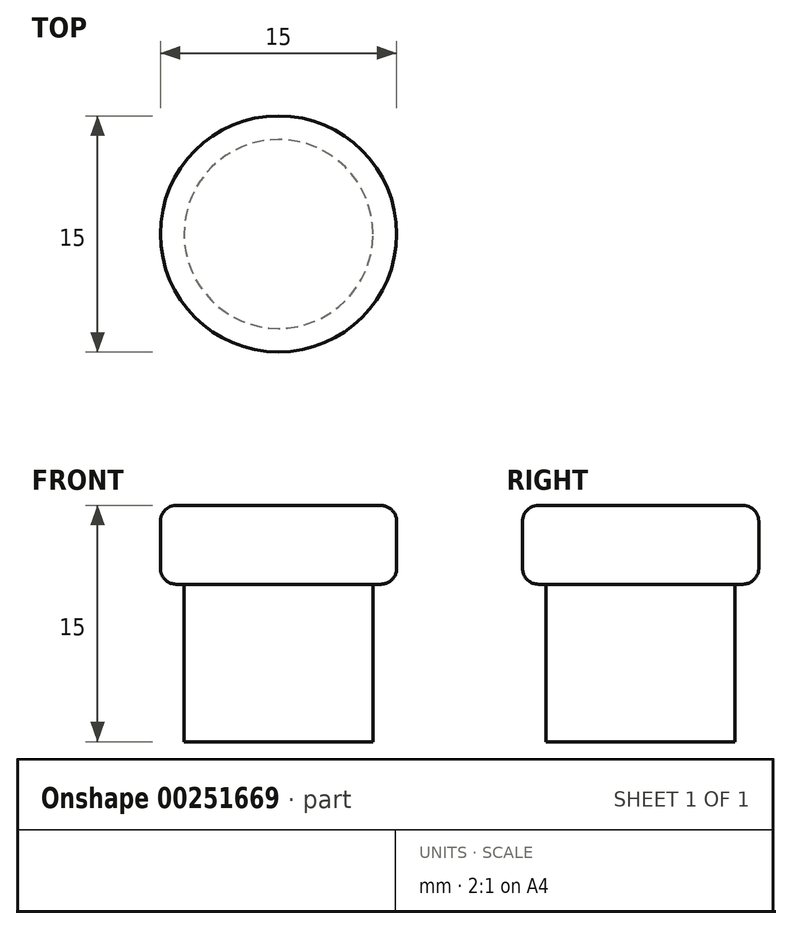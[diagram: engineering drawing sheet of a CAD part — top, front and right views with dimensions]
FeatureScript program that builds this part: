
annotation { "Feature Type Name" : "Feature", "Feature Type Description" : "" }
export const myFeature = defineFeature(function(context is Context, id is Id, definition is map)
    precondition{}
    {
        {
            var Q0;
            Q0=qCreatedBy(makeId("Top.planeOp"),FACE);
            var sketch = newSketch(context, id + "F0", { "sketchPlane" : qUnion([Q0])});
            skCircle(sketch, "E0", {"center": v(0, 0) * mm, "radius": 6 * mm});
            skSolve(sketch);
        }
        {
            var Q0;
            Q0 = qSketchRegion(id + "F0", true);
            extrude(context, id + "F1", {"entities" : qUnion([Q0]), "depth" : 10 * mm, "offsetDistance" : 25 * mm});
        }
        {
            var Q0;
            Q0=makeQuery(id+"F1.opExtrude","CAP_FACE",FACE,{"disambiguationData":[OSD([sQuery(id+"F0.wireOp",EDGE,"E0")])],"isStart":false});
            var sketch = newSketch(context, id + "F2", { "sketchPlane" : qUnion([Q0])});
            skCircle(sketch, "E1", {"center": v(0, 0) * mm, "radius": 7.5 * mm});
            skSolve(sketch);
        }
        {
            var Q0;
            Q0 = qSketchRegion(id + "F2", true);
            extrude(context, id + "F3", {"entities" : qUnion([Q0]), "operationType" : NewBodyOperationType.ADD, "depth" : 5 * mm, "offsetDistance" : 25 * mm});
        }
        {
            var Q0;
            Q0=makeQuery(id+"FBcZIfMRYgRZIZp_1.boolean.opBoolean","MERGE",EDGE,{"derivedFrom":[makeQuery(id+"F3.opExtrude","CAP_EDGE",EDGE,{"disambiguationData":[OSD([sQuery(id+"F2.wireOp",EDGE,"E1")])],"isStart":false}),makeQuery(id+"FBcZIfMRYgRZIZp_1.opRevolve","SWEPT_EDGE",EDGE,{"disambiguationData":[OSD([sQuery(id+"FvXkDSPQrULgmhM_1.wireOp",EDGE,"2eb79b60-172b-4c51-be24-07e29472f5c7.0"),sQuery(id+"FvXkDSPQrULgmhM_1.wireOp",EDGE,"2GFvvncA-9dK0-waaY-ttAt-wLxBZCuaZrCa")])]})]});
            var Q1;
            Q1=makeQuery(id+"F3.opExtrude","CAP_EDGE",EDGE,{"disambiguationData":[OSD([sQuery(id+"F2.wireOp",EDGE,"E1")])],"isStart":true});
            fillet(context, id + "F4", {"entities" : qUnion([Q0, Q1]), "radius" : 1 * mm, "tangentPropagation" : true, "allowEdgeOverflow" : false});
        }
    });
